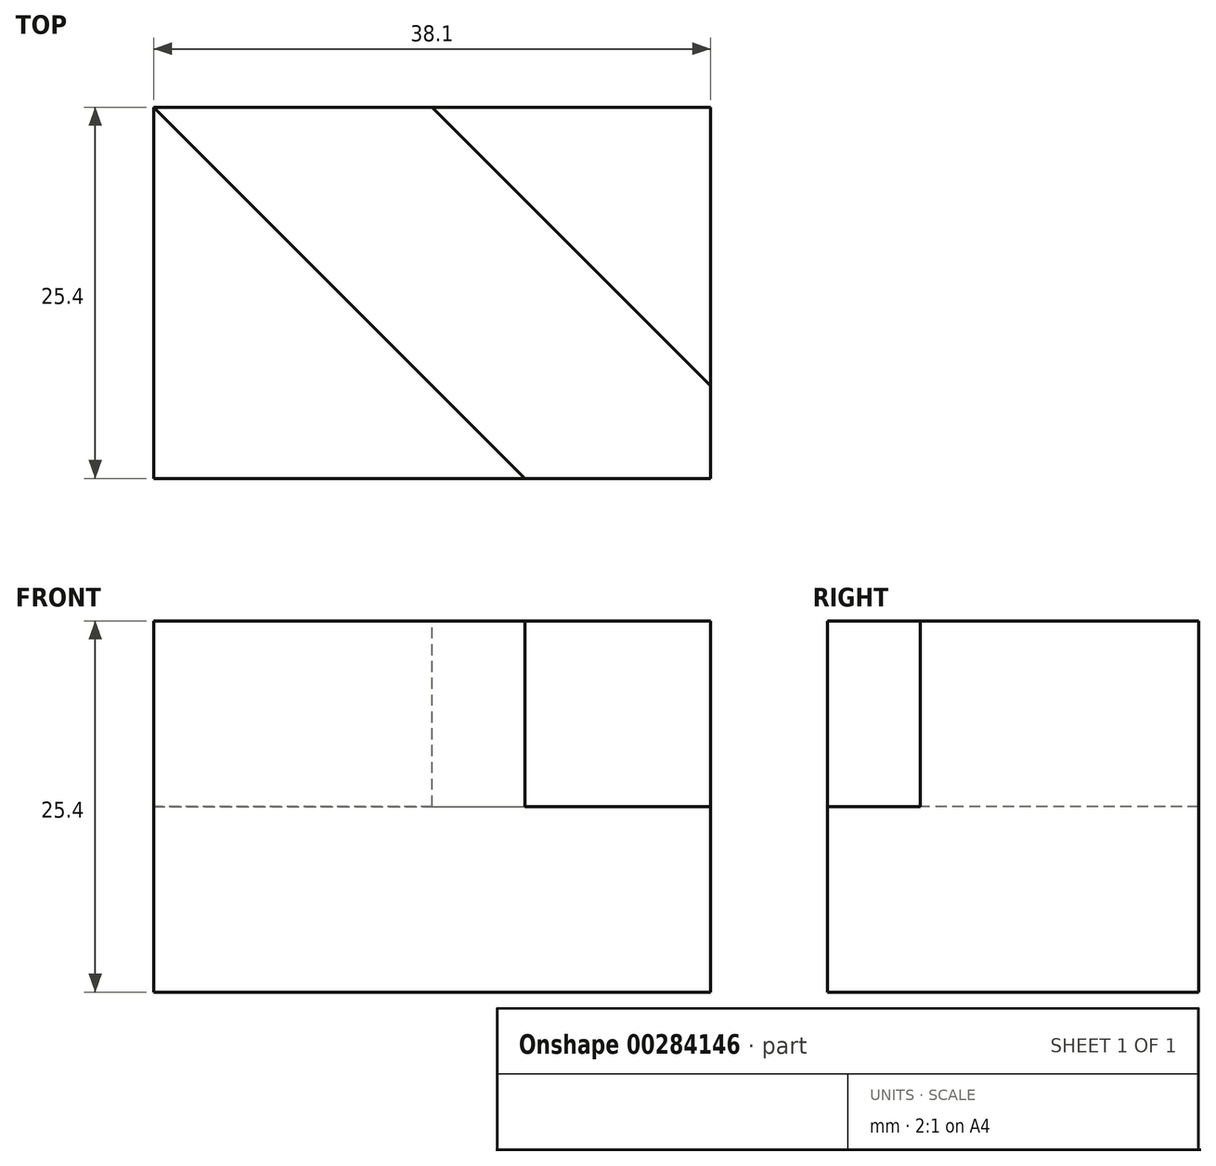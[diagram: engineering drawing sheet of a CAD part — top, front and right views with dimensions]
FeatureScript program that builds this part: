
annotation { "Feature Type Name" : "Feature", "Feature Type Description" : "" }
export const myFeature = defineFeature(function(context is Context, id is Id, definition is map)
    precondition{}
    {
        {
            var Q0;
            Q0=qCreatedBy(makeId("Front.planeOp"),FACE);
            var sketch = newSketch(context, id + "F0", { "sketchPlane" : qUnion([Q0])});
            skLineSegment(sketch, "E0.bottom", {"start": v(19.05, 12.7) * mm, "end": v(-19.05, 12.7) * mm});
            skLineSegment(sketch, "E0.top", {"start": v(19.05, -12.7) * mm, "end": v(-19.05, -12.7) * mm});
            skLineSegment(sketch, "E0.left", {"start": v(19.05, 12.7) * mm, "end": v(19.05, -12.7) * mm});
            skLineSegment(sketch, "E0.right", {"start": v(-19.05, 12.7) * mm, "end": v(-19.05, -12.7) * mm});
            skPoint(sketch, "E0.middle", {"position": v(0, 0) * mm});
            skSolve(sketch);
        }
        {
            var Q0;
            Q0=makeQuery(id+"F0.imprint","IMPRINT",FACE,{"disambiguationData":[TD([[makeQuery(id+"F0.imprint","IMPRINT",EDGE,{"derivedFrom":sQuery(id+"F0.wireOp",EDGE,"E0.bottom")}),1.0]])]});
            extrude(context, id + "F1", {"entities" : qUnion([Q0]), "endBound" : BoundingType.SYMMETRIC, "depth" : 25.4 * mm});
        }
        {
            var Q0;
            Q0=makeQuery(id+"F1.opExtrude","SWEPT_FACE",FACE,{"disambiguationData":[OSD([sQuery(id+"F0.wireOp",EDGE,"E0.bottom")])]});
            var sketch = newSketch(context, id + "F2", { "sketchPlane" : qUnion([Q0])});
            skLineSegment(sketch, "E1", {"start": v(-19.05, 12.7) * mm, "end": v(6.35, -12.7) * mm});
            skLineSegment(sketch, "E2", {"start": v(6.35, -12.7) * mm, "end": v(-19.05, -12.7) * mm});
            skLineSegment(sketch, "E3", {"start": v(-19.05, -12.7) * mm, "end": v(-19.05, 12.7) * mm});
            skLineSegment(sketch, "E4", {"start": v(0, 12.7) * mm, "end": v(19.05, -6.35) * mm});
            skLineSegment(sketch, "E5", {"start": v(19.05, -6.35) * mm, "end": v(19.05, 12.7) * mm});
            skLineSegment(sketch, "E6", {"start": v(19.05, 12.7) * mm, "end": v(0, 12.7) * mm});
            skSolve(sketch);
        }
        {
            var Q0;
            {var subQ0=sQuery(id+"F2.wireOp",EDGE,"E1");Q0=makeQuery(id+"F2.imprint","IMPRINT",FACE,{"disambiguationData":[TD([[makeQuery(id+"F2.imprint","IMPRINT",EDGE,{"derivedFrom":subQ0}),1.0]])]});}
            extrude(context, id + "F3", {"entities" : qUnion([Q0]), "operationType" : NewBodyOperationType.REMOVE, "oppositeDirection" : true, "depth" : 12.7 * mm});
        }
    });
